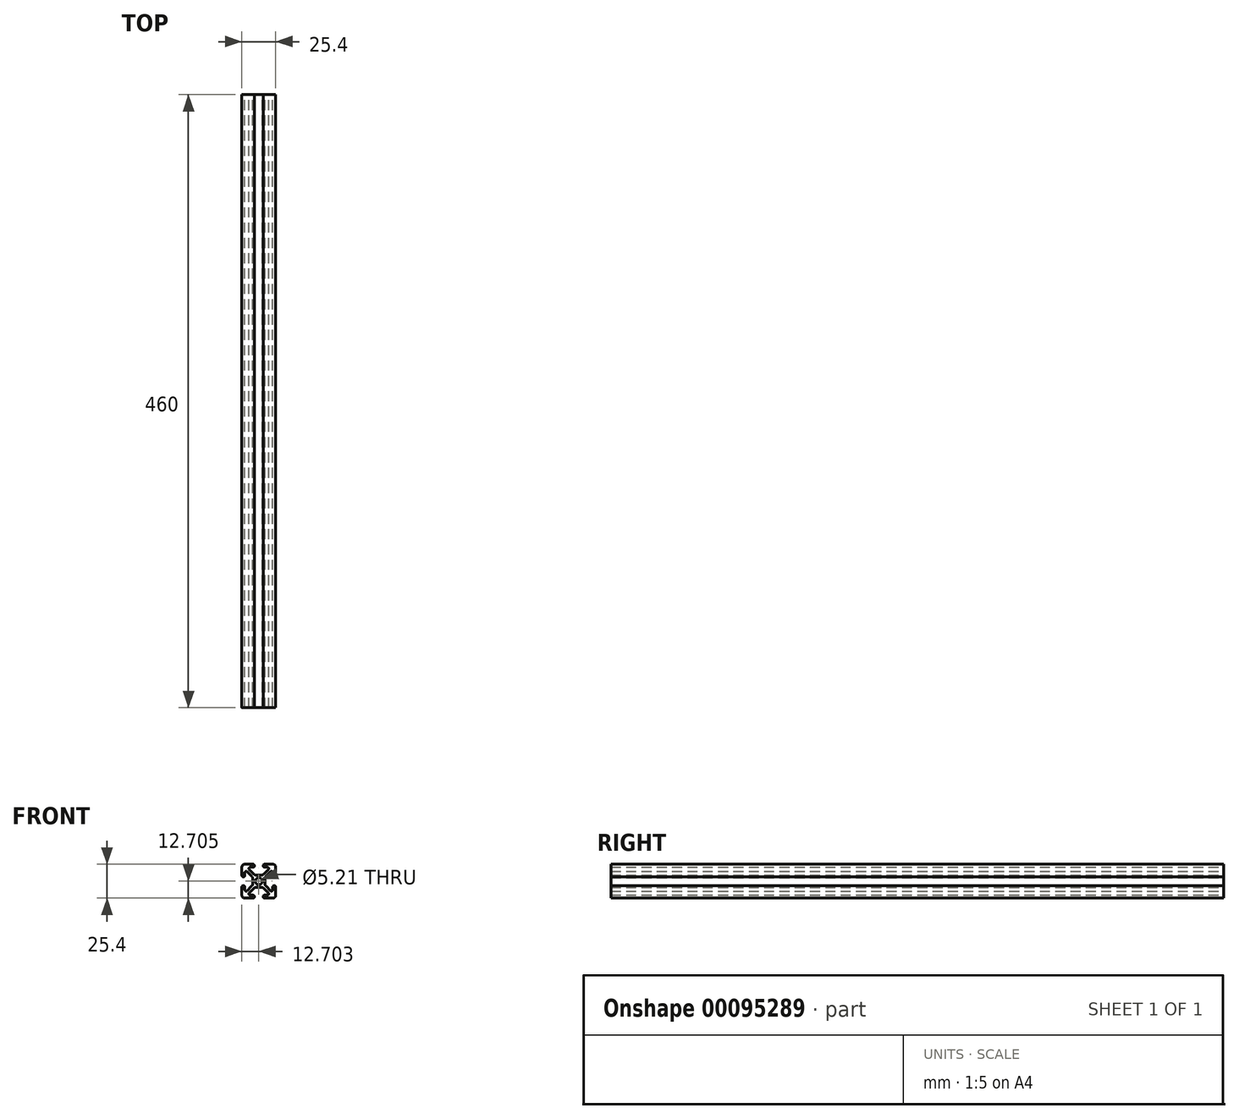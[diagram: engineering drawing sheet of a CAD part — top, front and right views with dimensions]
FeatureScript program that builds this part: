
annotation { "Feature Type Name" : "Feature", "Feature Type Description" : "" }
export const myFeature = defineFeature(function(context is Context, id is Id, definition is map)
    precondition{}
    {
        {
            var Q0;
            Q0=qCreatedBy(makeId("Front.planeOp"),FACE);
            var sketch = newSketch(context, id + "F0", { "sketchPlane" : qUnion([Q0])});
            skArc(sketch, "E0", {"start": v(-10.62, 12.76) * mm, "mid": v(-12.1, 12.15) * mm, "end": v(-12.73, 10.66) * mm});
            skArc(sketch, "E1", {"start": v(-12.73, 4.4) * mm, "mid": v(-11.62, 3.3) * mm, "end": v(-10.52, 4.4) * mm});
            skArc(sketch, "E2", {"start": v(-4.37, 10.55) * mm, "mid": v(-3.27, 11.66) * mm, "end": v(-4.37, 12.76) * mm});
            skArc(sketch, "E3", {"start": v(-8.75, 7.2) * mm, "mid": v(-9.88, 7.42) * mm, "end": v(-10.52, 6.46) * mm});
            skArc(sketch, "E4", {"start": v(-6.43, 10.55) * mm, "mid": v(-7.38, 9.92) * mm, "end": v(-7.16, 8.8) * mm});
            skLineSegment(sketch, "E5", {"start": v(-12.73, 10.66) * mm, "end": v(-12.73, 4.4) * mm});
            skLineSegment(sketch, "E6", {"start": v(-10.62, 12.76) * mm, "end": v(-4.37, 12.76) * mm});
            skLineSegment(sketch, "E7", {"start": v(-10.52, 4.4) * mm, "end": v(-10.52, 6.46) * mm});
            skLineSegment(sketch, "E8", {"start": v(-4.37, 10.55) * mm, "end": v(-6.43, 10.55) * mm});
            skLineSegment(sketch, "E9", {"start": v(-11.51, 7.5) * mm, "end": v(-10.3, 7.5) * mm, "construction": true});
            skLineSegment(sketch, "E10", {"start": v(-13.64, 3.3) * mm, "end": v(-12.36, 3.3) * mm, "construction": true});
            skLineSegment(sketch, "E11", {"start": v(-7.46, 11.03) * mm, "end": v(-7.46, 8.91) * mm, "construction": true});
            skLineSegment(sketch, "E12", {"start": v(-3.27, 12.37) * mm, "end": v(-3.27, 10.25) * mm, "construction": true});
            skLineSegment(sketch, "E13.bottom", {"start": v(1.57, 4.57) * mm, "end": v(-1.63, 4.57) * mm});
            skLineSegment(sketch, "E13.top", {"start": v(1.57, -4.44) * mm, "end": v(-1.63, -4.44) * mm});
            skLineSegment(sketch, "E13.left", {"start": v(4.48, 1.66) * mm, "end": v(4.48, -1.53) * mm});
            skLineSegment(sketch, "E13.right", {"start": v(-4.54, 1.66) * mm, "end": v(-4.54, -1.53) * mm});
            skPoint(sketch, "E13.middle", {"position": v(-0.03, 0.06) * mm});
            skLineSegment(sketch, "E14", {"start": v(-8.75, 7.2) * mm, "end": v(-5.47, 3.9) * mm});
            skLineSegment(sketch, "E15", {"start": v(-7.16, 8.8) * mm, "end": v(-3.87, 5.5) * mm});
            skArc(sketch, "E16.filletArc", {"start": v(-3.87, 5.5) * mm, "mid": v(-2.84, 4.81) * mm, "end": v(-1.63, 4.57) * mm});
            skArc(sketch, "E17.filletArc", {"start": v(-4.54, 1.66) * mm, "mid": v(-4.78, 2.88) * mm, "end": v(-5.47, 3.9) * mm});
            skLineSegment(sketch, "E18", {"start": v(5.32, 0.06) * mm, "end": v(-7.21, 0.06) * mm, "construction": true});
            skPoint(sketch, "E18.startSnap0", {"position": v(2.97, 0.06) * mm});
            skPoint(sketch, "E19", {"position": v(-0.03, -4.44) * mm});
            skLineSegment(sketch, "E20", {"start": v(-0.03, -6.76) * mm, "end": v(-0.03, 5.83) * mm, "construction": true});
            skLineSegment(sketch, "E21.MirrorCS", {"start": v(11.46, 7.5) * mm, "end": v(10.25, 7.5) * mm, "construction": true});
            skArc(sketch, "E22.MirrorCS", {"start": v(10.57, 12.76) * mm, "mid": v(12.06, 12.15) * mm, "end": v(12.67, 10.66) * mm});
            skLineSegment(sketch, "E23.MirrorCS", {"start": v(7.4, 11.03) * mm, "end": v(7.4, 8.91) * mm, "construction": true});
            skLineSegment(sketch, "E24.MirrorCS", {"start": v(10.46, 4.4) * mm, "end": v(10.46, 6.46) * mm});
            skArc(sketch, "E25.MirrorCS", {"start": v(3.82, 5.5) * mm, "mid": v(2.79, 4.81) * mm, "end": v(1.57, 4.57) * mm});
            skLineSegment(sketch, "E26.MirrorCS", {"start": v(8.7, 7.2) * mm, "end": v(5.41, 3.9) * mm});
            skLineSegment(sketch, "E27.MirrorCS", {"start": v(3.21, 12.37) * mm, "end": v(3.21, 10.25) * mm, "construction": true});
            skLineSegment(sketch, "E28.MirrorCS", {"start": v(13.58, 3.3) * mm, "end": v(12.3, 3.3) * mm, "construction": true});
            skArc(sketch, "E29.MirrorCS", {"start": v(4.32, 10.55) * mm, "mid": v(3.21, 11.66) * mm, "end": v(4.32, 12.76) * mm});
            skArc(sketch, "E30.MirrorCS", {"start": v(8.7, 7.2) * mm, "mid": v(9.83, 7.42) * mm, "end": v(10.46, 6.46) * mm});
            skArc(sketch, "E31.MirrorCS", {"start": v(12.67, 4.4) * mm, "mid": v(11.57, 3.3) * mm, "end": v(10.46, 4.4) * mm});
            skLineSegment(sketch, "E32.MirrorCS", {"start": v(10.57, 12.76) * mm, "end": v(4.32, 12.76) * mm});
            skLineSegment(sketch, "E33.MirrorCS", {"start": v(12.67, 10.66) * mm, "end": v(12.67, 4.4) * mm});
            skArc(sketch, "E34.MirrorCS", {"start": v(6.37, 10.55) * mm, "mid": v(7.33, 9.92) * mm, "end": v(7.1, 8.8) * mm});
            skLineSegment(sketch, "E35.MirrorCS", {"start": v(7.1, 8.8) * mm, "end": v(3.82, 5.5) * mm});
            skLineSegment(sketch, "E36.MirrorCS", {"start": v(4.32, 10.55) * mm, "end": v(6.37, 10.55) * mm});
            skArc(sketch, "E37.MirrorCS", {"start": v(4.48, 1.66) * mm, "mid": v(4.72, 2.88) * mm, "end": v(5.41, 3.9) * mm});
            skLineSegment(sketch, "E38.MirrorCS", {"start": v(-11.51, -7.37) * mm, "end": v(-10.3, -7.37) * mm, "construction": true});
            skArc(sketch, "E39.MirrorCS", {"start": v(-3.87, -5.37) * mm, "mid": v(-2.84, -4.69) * mm, "end": v(-1.63, -4.44) * mm});
            skArc(sketch, "E40.MirrorCS", {"start": v(-10.62, -12.64) * mm, "mid": v(-12.1, -12.02) * mm, "end": v(-12.73, -10.53) * mm});
            skArc(sketch, "E41.MirrorCS", {"start": v(-8.75, -7.07) * mm, "mid": v(-9.88, -7.3) * mm, "end": v(-10.52, -6.33) * mm});
            skArc(sketch, "E42.MirrorCS", {"start": v(-6.43, -10.43) * mm, "mid": v(-7.38, -9.79) * mm, "end": v(-7.16, -8.66) * mm});
            skLineSegment(sketch, "E43.MirrorCS", {"start": v(-3.27, -12.24) * mm, "end": v(-3.27, -10.12) * mm, "construction": true});
            skArc(sketch, "E44.MirrorCS", {"start": v(-4.54, -1.53) * mm, "mid": v(-4.78, -2.75) * mm, "end": v(-5.47, -3.78) * mm});
            skLineSegment(sketch, "E45.MirrorCS", {"start": v(-12.73, -10.53) * mm, "end": v(-12.73, -4.28) * mm});
            skLineSegment(sketch, "E46.MirrorCS", {"start": v(-13.64, -3.17) * mm, "end": v(-12.36, -3.17) * mm, "construction": true});
            skLineSegment(sketch, "E47.MirrorCS", {"start": v(-7.46, -10.9) * mm, "end": v(-7.46, -8.78) * mm, "construction": true});
            skLineSegment(sketch, "E48.MirrorCS", {"start": v(-4.37, -10.43) * mm, "end": v(-6.43, -10.43) * mm});
            skLineSegment(sketch, "E49.MirrorCS", {"start": v(-10.62, -12.64) * mm, "end": v(-4.37, -12.64) * mm});
            skLineSegment(sketch, "E50.MirrorCS", {"start": v(-10.52, -4.28) * mm, "end": v(-10.52, -6.33) * mm});
            skArc(sketch, "E51.MirrorCS", {"start": v(-12.73, -4.28) * mm, "mid": v(-11.62, -3.17) * mm, "end": v(-10.52, -4.28) * mm});
            skLineSegment(sketch, "E52.MirrorCS", {"start": v(-8.75, -7.07) * mm, "end": v(-5.47, -3.78) * mm});
            skLineSegment(sketch, "E53.MirrorCS", {"start": v(-7.16, -8.66) * mm, "end": v(-3.87, -5.37) * mm});
            skArc(sketch, "E54.MirrorCS", {"start": v(-4.37, -10.43) * mm, "mid": v(-3.27, -11.53) * mm, "end": v(-4.37, -12.64) * mm});
            skLineSegment(sketch, "E55.MirrorCS", {"start": v(11.46, -7.37) * mm, "end": v(10.25, -7.37) * mm, "construction": true});
            skArc(sketch, "E56.MirrorCS", {"start": v(4.32, -10.43) * mm, "mid": v(3.21, -11.53) * mm, "end": v(4.32, -12.64) * mm});
            skLineSegment(sketch, "E57.MirrorCS", {"start": v(13.58, -3.17) * mm, "end": v(12.3, -3.17) * mm, "construction": true});
            skArc(sketch, "E58.MirrorCS", {"start": v(8.7, -7.07) * mm, "mid": v(9.83, -7.3) * mm, "end": v(10.46, -6.33) * mm});
            skLineSegment(sketch, "E59.MirrorCS", {"start": v(7.1, -8.66) * mm, "end": v(3.82, -5.37) * mm});
            skLineSegment(sketch, "E60.MirrorCS", {"start": v(7.4, -10.9) * mm, "end": v(7.4, -8.78) * mm, "construction": true});
            skLineSegment(sketch, "E61.MirrorCS", {"start": v(3.21, -12.24) * mm, "end": v(3.21, -10.12) * mm, "construction": true});
            skLineSegment(sketch, "E62.MirrorCS", {"start": v(4.32, -10.43) * mm, "end": v(6.37, -10.43) * mm});
            skArc(sketch, "E63.MirrorCS", {"start": v(3.82, -5.37) * mm, "mid": v(2.79, -4.69) * mm, "end": v(1.57, -4.44) * mm});
            skArc(sketch, "E64.MirrorCS", {"start": v(10.57, -12.64) * mm, "mid": v(12.06, -12.02) * mm, "end": v(12.67, -10.53) * mm});
            skLineSegment(sketch, "E65.MirrorCS", {"start": v(10.57, -12.64) * mm, "end": v(4.32, -12.64) * mm});
            skLineSegment(sketch, "E66.MirrorCS", {"start": v(8.7, -7.07) * mm, "end": v(5.41, -3.78) * mm});
            skLineSegment(sketch, "E67.MirrorCS", {"start": v(12.67, -10.53) * mm, "end": v(12.67, -4.28) * mm});
            skArc(sketch, "E68.MirrorCS", {"start": v(12.67, -4.28) * mm, "mid": v(11.57, -3.17) * mm, "end": v(10.46, -4.28) * mm});
            skArc(sketch, "E69.MirrorCS", {"start": v(4.48, -1.53) * mm, "mid": v(4.72, -2.75) * mm, "end": v(5.41, -3.78) * mm});
            skLineSegment(sketch, "E70.MirrorCS", {"start": v(10.46, -4.28) * mm, "end": v(10.46, -6.33) * mm});
            skArc(sketch, "E71.MirrorCS", {"start": v(6.37, -10.43) * mm, "mid": v(7.33, -9.79) * mm, "end": v(7.1, -8.66) * mm});
            skCircle(sketch, "E72", {"center": v(-0.03, 0.06) * mm, "radius": 2.6 * mm});
            skSolve(sketch);
        }
        {
            var Q0;
            Q0=qSketchRegion(id+"F0",true);
            extrude(context, id + "F1", {"entities" : qUnion([Q0]), "depth" : 460 * mm});
        }
    });
